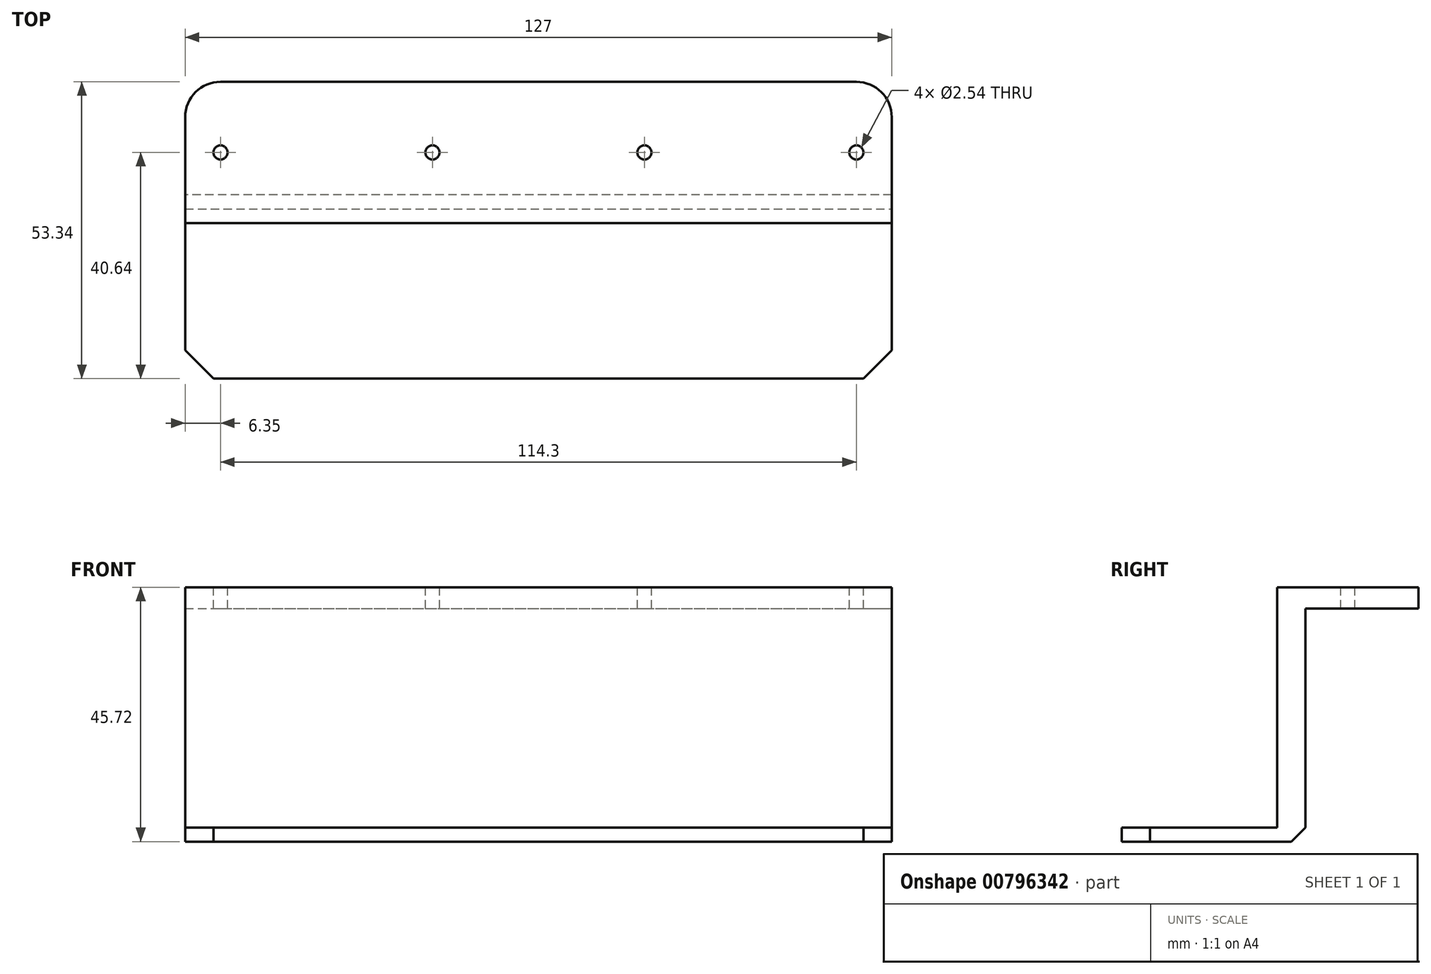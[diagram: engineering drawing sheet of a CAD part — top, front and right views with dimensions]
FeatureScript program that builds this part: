
annotation { "Feature Type Name" : "Feature", "Feature Type Description" : "" }
export const myFeature = defineFeature(function(context is Context, id is Id, definition is map)
    precondition{}
    {
        {
            var Q0;
            Q0=qCreatedBy(makeId("Right.planeOp"),FACE);
            var sketch = newSketch(context, id + "F0", { "sketchPlane" : qUnion([Q0])});
            skLineSegment(sketch, "E0", {"start": v(0, 0) * mm, "end": v(33.02, 0) * mm});
            skLineSegment(sketch, "E1", {"start": v(33.02, 0) * mm, "end": v(33.02, 41.91) * mm});
            skLineSegment(sketch, "E2", {"start": v(33.02, 41.91) * mm, "end": v(53.34, 41.91) * mm});
            skLineSegment(sketch, "E3", {"start": v(53.34, 41.91) * mm, "end": v(53.34, 45.72) * mm});
            skLineSegment(sketch, "E4", {"start": v(53.34, 45.72) * mm, "end": v(27.94, 45.72) * mm});
            skLineSegment(sketch, "E5", {"start": v(27.94, 45.72) * mm, "end": v(27.94, 2.54) * mm});
            skLineSegment(sketch, "E6", {"start": v(27.94, 2.54) * mm, "end": v(0, 2.54) * mm});
            skLineSegment(sketch, "E7", {"start": v(0, 2.54) * mm, "end": v(0, 0) * mm});
            skSolve(sketch);
        }
        {
            var Q0;
            Q0 = qSketchRegion(id + "F0", true);
            extrude(context, id + "F1", {"entities" : qUnion([Q0]), "oppositeDirection" : true, "depth" : 127 * mm, "offsetDistance" : 25.4 * mm});
        }
        {
            var Q0;
            Q0=makeQuery(id+"F1.opExtrude","CAP_EDGE",EDGE,{"disambiguationData":[OSD([sQuery(id+"F0.wireOp",EDGE,"E7")])],"isStart":true});
            var Q1;
            Q1=makeQuery(id+"F1.opExtrude","CAP_EDGE",EDGE,{"disambiguationData":[OSD([sQuery(id+"F0.wireOp",EDGE,"E7")])],"isStart":false});
            chamfer(context, id + "F2", {"entities" : qUnion([Q0, Q1]), "width" : 5.08 * mm, "tangentPropagation" : true});
        }
        {
            var Q0;
            Q0=makeQuery(id+"F1.opExtrude","SWEPT_FACE",FACE,{"disambiguationData":[OSD([sQuery(id+"F0.wireOp",EDGE,"E4")])]});
            var sketch = newSketch(context, id + "F3", { "sketchPlane" : qUnion([Q0])});
            skPoint(sketch, "E8", {"position": v(-120.65, 40.64) * mm});
            skPoint(sketch, "E8.positionSnap0", {"position": v(-127, 40.64) * mm});
            skPoint(sketch, "E9", {"position": v(-82.55, 40.64) * mm});
            skPoint(sketch, "E10", {"position": v(-44.45, 40.64) * mm});
            skPoint(sketch, "E11", {"position": v(-6.35, 40.64) * mm});
            skSolve(sketch);
        }
        {
            var Q0;
            Q0=sQuery(id+"F3.wireOp",VERTEX,"E8");
            var Q1;
            Q1=sQuery(id+"F3.wireOp",VERTEX,"E9");
            var Q2;
            Q2=sQuery(id+"F3.wireOp",VERTEX,"E10");
            var Q3;
            Q3=sQuery(id+"F3.wireOp",VERTEX,"E11");
            var Q4;
            Q4=makeQuery(id+"F1.opExtrude","SWEPT_BODY",BODY,{"disambiguationData":[OSD([sQuery(id+"F0.wireOp",EDGE,"E0"),sQuery(id+"F0.wireOp",EDGE,"E1"),sQuery(id+"F0.wireOp",EDGE,"E2"),sQuery(id+"F0.wireOp",EDGE,"E3"),sQuery(id+"F0.wireOp",EDGE,"E4"),sQuery(id+"F0.wireOp",EDGE,"E5"),sQuery(id+"F0.wireOp",EDGE,"E6"),sQuery(id+"F0.wireOp",EDGE,"E7")])]});
            hole(context, id + "F4", {"style" : HoleStyle.SIMPLE, "endStyle" : HoleEndStyle.THROUGH, "holeDiameter" : 2.54 * mm, "majorDiameter" : 6.35 * mm, "isTappedThrough" : true, "tappedDepth" : 12.7 * mm, "tapClearance" : 3, "locations" : qUnion([Q0, Q1, Q2, Q3]), "scope" : qUnion([Q4])});
        }
        {
            var Q0;
            Q0=makeQuery(id+"F1.opExtrude","CAP_EDGE",EDGE,{"disambiguationData":[OSD([sQuery(id+"F0.wireOp",EDGE,"E3")])],"isStart":true});
            var Q1;
            Q1=makeQuery(id+"F1.opExtrude","CAP_EDGE",EDGE,{"disambiguationData":[OSD([sQuery(id+"F0.wireOp",EDGE,"E3")])],"isStart":false});
            fillet(context, id + "F5", {"entities" : qUnion([Q0, Q1]), "radius" : 6.35 * mm, "tangentPropagation" : true, "allowEdgeOverflow" : false});
        }
        {
            var Q0;
            Q0=makeQuery(id+"F1.opExtrude","SWEPT_EDGE",EDGE,{"disambiguationData":[OSD([sQuery(id+"F0.wireOp",EDGE,"E0"),sQuery(id+"F0.wireOp",EDGE,"E1")])]});
            chamfer(context, id + "F6", {"entities" : qUnion([Q0]), "width" : 2.54 * mm, "tangentPropagation" : true});
        }
    });
